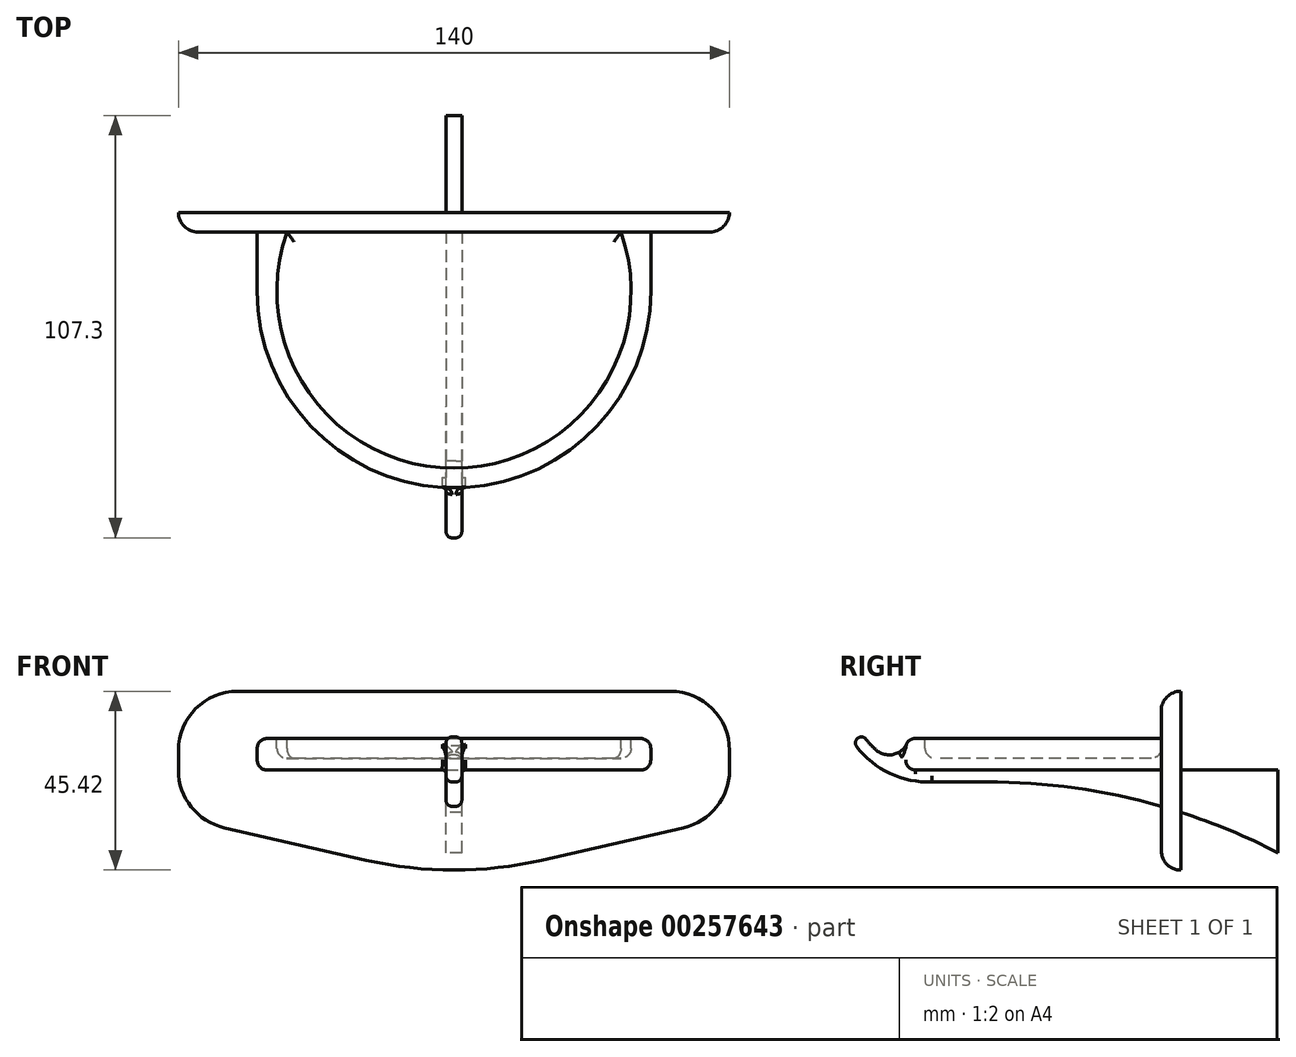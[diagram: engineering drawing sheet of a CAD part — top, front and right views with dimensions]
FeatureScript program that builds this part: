
annotation { "Feature Type Name" : "Feature", "Feature Type Description" : "" }
export const myFeature = defineFeature(function(context is Context, id is Id, definition is map)
    precondition{}
    {
        {
            var Q0;
            Q0=qCreatedBy(makeId("Front.planeOp"),FACE);
            var sketch = newSketch(context, id + "F0", { "sketchPlane" : qUnion([Q0])});
            skLineSegment(sketch, "E0.bottom", {"start": v(-55, 12) * mm, "end": v(55, 12) * mm});
            skLineSegment(sketch, "E0.left", {"start": v(-70, -3) * mm, "end": v(-70, -8.04) * mm});
            skLineSegment(sketch, "E0.right", {"start": v(70, -3) * mm, "end": v(70, -8.04) * mm});
            skLineSegment(sketch, "E1", {"start": v(-58.34, -22.66) * mm, "end": v(-22.28, -30.9) * mm});
            skLineSegment(sketch, "E2", {"start": v(22.28, -30.9) * mm, "end": v(58.34, -22.66) * mm});
            skPoint(sketch, "E3.visualSharp", {"position": v(-70, 12) * mm});
            skArc(sketch, "E3.filletArc", {"start": v(-55, 12) * mm, "mid": v(-65.6, 7.6) * mm, "end": v(-70, -3) * mm});
            skPoint(sketch, "E4.visualSharp", {"position": v(-70, -20) * mm});
            skArc(sketch, "E4.filletArc", {"start": v(-70, -8.04) * mm, "mid": v(-66.73, -17.4) * mm, "end": v(-58.34, -22.66) * mm});
            skPoint(sketch, "E5.visualSharp", {"position": v(70, 12) * mm});
            skArc(sketch, "E5.filletArc", {"start": v(70, -3) * mm, "mid": v(65.6, 7.6) * mm, "end": v(55, 12) * mm});
            skPoint(sketch, "E6.visualSharp", {"position": v(70, -20) * mm});
            skArc(sketch, "E6.filletArc", {"start": v(58.34, -22.66) * mm, "mid": v(66.73, -17.4) * mm, "end": v(70, -8.04) * mm});
            skPoint(sketch, "E7.visualSharp", {"position": v(0, -36) * mm});
            skArc(sketch, "E7.filletArc", {"start": v(-22.28, -30.9) * mm, "mid": v(0, -33.42) * mm, "end": v(22.28, -30.9) * mm});
            skSolve(sketch);
        }
        {
            var Q0;
            Q0=makeQuery(id+"F0.imprint","IMPRINT",FACE,{"disambiguationData":[TD([[makeQuery(id+"F0.imprint","IMPRINT",EDGE,{"derivedFrom":sQuery(id+"F0.wireOp",EDGE,"E0.bottom")}),-1.0]])]});
            extrude(context, id + "F1", {"entities" : qUnion([Q0]), "depth" : 5 * mm});
        }
        {
            var Q0;
            Q0=makeQuery(id+"F1.opExtrude","CAP_EDGE",EDGE,{"disambiguationData":[OSD([sQuery(id+"F0.wireOp",EDGE,"E0.bottom")])],"isStart":false});
            fillet(context, id + "F2", {"entities" : qUnion([Q0]), "radius" : 5 * mm, "tangentPropagation" : true, "allowEdgeOverflow" : false});
        }
        {
            var Q0;
            Q0=qCreatedBy(makeId("Top.planeOp"),FACE);
            var sketch = newSketch(context, id + "F3", { "sketchPlane" : qUnion([Q0])});
            skArc(sketch, "E8", {"start": v(-50, -20) * mm, "mid": v(0, -70) * mm, "end": v(50, -20) * mm});
            skLineSegment(sketch, "E9", {"start": v(50, -5) * mm, "end": v(50, -20) * mm});
            skLineSegment(sketch, "E10", {"start": v(-50, -5) * mm, "end": v(-50, -20) * mm});
            skLineSegment(sketch, "E11", {"start": v(50, -5) * mm, "end": v(-50, -5) * mm});
            skSolve(sketch);
        }
        {
            var Q0;
            Q0=makeQuery(id+"F3.imprint","IMPRINT",FACE,{"disambiguationData":[TD([[makeQuery(id+"F3.imprint","IMPRINT",EDGE,{"derivedFrom":sQuery(id+"F3.wireOp",EDGE,"E8")}),1.0]])]});
            extrude(context, id + "F4", {"entities" : qUnion([Q0]), "operationType" : NewBodyOperationType.ADD, "oppositeDirection" : true, "depth" : 8 * mm});
        }
        {
            var Q0;
            Q0=makeQuery(id+"F4.opExtrude","CAP_FACE",FACE,{"disambiguationData":[OSD([sQuery(id+"F3.wireOp",EDGE,"E8"),sQuery(id+"F3.wireOp",EDGE,"E9"),sQuery(id+"F3.wireOp",EDGE,"E10"),sQuery(id+"F3.wireOp",EDGE,"E11")])],"isStart":true});
            var sketch = newSketch(context, id + "F5", { "sketchPlane" : qUnion([Q0])});
            skArc(sketch, "E12", {"start": v(-42.43, -5) * mm, "mid": v(0, -65) * mm, "end": v(42.43, -5) * mm});
            skLineSegment(sketch, "E13", {"start": v(-42.43, -5) * mm, "end": v(42.43, -5) * mm});
            skSolve(sketch);
        }
        {
            var Q0;
            Q0=makeQuery(id+"F5.imprint","IMPRINT",FACE,{"disambiguationData":[TD([[makeQuery(id+"F5.imprint","IMPRINT",EDGE,{"derivedFrom":sQuery(id+"F5.wireOp",EDGE,"E12")}),1.0]])]});
            extrude(context, id + "F6", {"entities" : qUnion([Q0]), "operationType" : NewBodyOperationType.REMOVE, "oppositeDirection" : true, "depth" : 5 * mm});
        }
        {
            var Q0;
            Q0=makeQuery(id+"F6.boolean.opBoolean","COPY",EDGE,{"derivedFrom":makeQuery(id+"F6.opExtrude","CAP_EDGE",EDGE,{"disambiguationData":[OSD([sQuery(id+"F5.wireOp",EDGE,"E12")])],"isStart":true})});
            var Q1;
            Q1=makeQuery(id+"F4.opExtrude","CAP_EDGE",EDGE,{"disambiguationData":[OSD([sQuery(id+"F3.wireOp",EDGE,"E8")])],"isStart":true});
            var Q2;
            Q2=makeQuery(id+"F4.opExtrude","CAP_EDGE",EDGE,{"disambiguationData":[OSD([sQuery(id+"F3.wireOp",EDGE,"E10")])],"isStart":false});
            var Q3;
            Q3=makeQuery(id+"F6.boolean.opBoolean","COPY",EDGE,{"derivedFrom":makeQuery(id+"F6.opExtrude","CAP_EDGE",EDGE,{"disambiguationData":[OSD([sQuery(id+"F5.wireOp",EDGE,"E12")])],"isStart":false})});
            var Q4;
            Q4=makeQuery(id+"F6.boolean.opBoolean","COPY",EDGE,{"derivedFrom":makeQuery(id+"F6.opExtrude","CAP_EDGE",EDGE,{"disambiguationData":[OSD([sQuery(id+"F5.wireOp",EDGE,"E13")])],"isStart":false})});
            var Q5;
            {var subQ0=sQuery(id+"F3.wireOp",EDGE,"E10");var subQ1=sQuery(id+"F3.wireOp",EDGE,"E11");Q5=makeQuery(id+"F6.boolean.opBoolean","SPLIT",EDGE,{"disambiguationData":[TD([makeQuery(id+"F4.opExtrude","SWEPT_FACE",FACE,{"disambiguationData":[OSD([subQ0])]})])],"derivedFrom":makeQuery(id+"F4.opExtrude","CAP_EDGE",EDGE,{"disambiguationData":[OSD([subQ1])],"isStart":true})});}
            fillet(context, id + "F7", {"entities" : qUnion([Q0, Q1, Q2, Q3, Q4, Q5]), "radius" : 2.5 * mm, "tangentPropagation" : true, "allowEdgeOverflow" : false});
        }
        {
            var Q0;
            Q0=qCreatedBy(makeId("Right.planeOp"),FACE);
            var sketch = newSketch(context, id + "F8", { "sketchPlane" : qUnion([Q0])});
            skArc(sketch, "E14.MirrorCS", {"start": v(-79.99, -0.2) * mm, "mid": v(-82.09, 0.1) * mm, "end": v(-82.39, -2) * mm});
            skArc(sketch, "E15.MirrorCS", {"start": v(-77.35, -3) * mm, "mid": v(-78.75, -1.67) * mm, "end": v(-79.99, -0.2) * mm});
            skArc(sketch, "E16.MirrorCS", {"start": v(-69.83, -1.73) * mm, "mid": v(-73.3, -4.1) * mm, "end": v(-77.35, -3) * mm});
            skLineSegment(sketch, "E17.MirrorCS", {"start": v(-65.39, -8) * mm, "end": v(-69.83, -1.73) * mm});
            skLineSegment(sketch, "E18.MirrorCS", {"start": v(24.61, -29) * mm, "end": v(24.61, -8) * mm});
            skLineSegment(sketch, "E19.MirrorCS", {"start": v(24.61, -8) * mm, "end": v(-65.39, -8) * mm});
            skArc(sketch, "E20", {"start": v(-82.39, -2) * mm, "mid": v(-73.92, -8.9) * mm, "end": v(-63.2, -11) * mm});
            skLineSegment(sketch, "E21", {"start": v(-63.2, -11) * mm, "end": v(-49.37, -11) * mm});
            skArc(sketch, "E22", {"start": v(-49.37, -11) * mm, "mid": v(-11.3, -15.56) * mm, "end": v(24.61, -29) * mm});
            skSolve(sketch);
        }
        {
            var Q0;
            Q0=makeQuery(id+"F8.imprint","IMPRINT",FACE,{"disambiguationData":[TD([[makeQuery(id+"F8.imprint","IMPRINT",EDGE,{"derivedFrom":sQuery(id+"F8.wireOp",EDGE,"E14.MirrorCS")}),1.0]])]});
            extrude(context, id + "F9", {"entities" : qUnion([Q0]), "operationType" : NewBodyOperationType.ADD, "depth" : 4 * mm, "offsetDistance" : 25 * mm, "symmetric" : true});
        }
        {
            var Q0;
            Q0=makeQuery(id+"F9.boolean.opBoolean","INTERSECT",EDGE,{"derivedFrom":[makeQuery(id+"F4.opExtrude","CAP_FACE",FACE,{"disambiguationData":[OSD([sQuery(id+"F3.wireOp",EDGE,"E8"),sQuery(id+"F3.wireOp",EDGE,"E9"),sQuery(id+"F3.wireOp",EDGE,"E10"),sQuery(id+"F3.wireOp",EDGE,"E11")])],"isStart":false}),makeQuery(id+"F9.opExtrude","CAP_FACE",FACE,{"disambiguationData":[OSD([sQuery(id+"F8.wireOp",EDGE,"3d30b8ef-365d-4eac-9476-35001526b1a10.MirrorCS"),sQuery(id+"F8.wireOp",EDGE,"E14.MirrorCS"),sQuery(id+"F8.wireOp",EDGE,"E15.MirrorCS"),sQuery(id+"F8.wireOp",EDGE,"3d30b8ef-365d-4eac-9476-35001526b1a13.MirrorCS"),sQuery(id+"F8.wireOp",EDGE,"3d30b8ef-365d-4eac-9476-35001526b1a14.MirrorCS"),sQuery(id+"F8.wireOp",EDGE,"E16.MirrorCS"),sQuery(id+"F8.wireOp",EDGE,"E17.MirrorCS"),sQuery(id+"F8.wireOp",EDGE,"E18.MirrorCS"),sQuery(id+"F8.wireOp",EDGE,"E19.MirrorCS"),sQuery(id+"F8.wireOp",EDGE,"3d30b8ef-365d-4eac-9476-35001526b1a19.MirrorCS")])],"isStart":true})]});
            var Q1;
            Q1=makeQuery(id+"F9.boolean.opBoolean","INTERSECT",EDGE,{"derivedFrom":[makeQuery(id+"F4.opExtrude","CAP_FACE",FACE,{"disambiguationData":[OSD([sQuery(id+"F3.wireOp",EDGE,"E8"),sQuery(id+"F3.wireOp",EDGE,"E9"),sQuery(id+"F3.wireOp",EDGE,"E10"),sQuery(id+"F3.wireOp",EDGE,"E11")])],"isStart":false}),makeQuery(id+"F9.opExtrude","CAP_FACE",FACE,{"disambiguationData":[OSD([sQuery(id+"F8.wireOp",EDGE,"3d30b8ef-365d-4eac-9476-35001526b1a10.MirrorCS"),sQuery(id+"F8.wireOp",EDGE,"E14.MirrorCS"),sQuery(id+"F8.wireOp",EDGE,"E15.MirrorCS"),sQuery(id+"F8.wireOp",EDGE,"3d30b8ef-365d-4eac-9476-35001526b1a13.MirrorCS"),sQuery(id+"F8.wireOp",EDGE,"3d30b8ef-365d-4eac-9476-35001526b1a14.MirrorCS"),sQuery(id+"F8.wireOp",EDGE,"E16.MirrorCS"),sQuery(id+"F8.wireOp",EDGE,"E17.MirrorCS"),sQuery(id+"F8.wireOp",EDGE,"E18.MirrorCS"),sQuery(id+"F8.wireOp",EDGE,"E19.MirrorCS"),sQuery(id+"F8.wireOp",EDGE,"3d30b8ef-365d-4eac-9476-35001526b1a19.MirrorCS")])],"isStart":false})]});
            fillet(context, id + "F10", {"entities" : qUnion([Q0, Q1]), "radius" : 1 * mm, "tangentPropagation" : true, "allowEdgeOverflow" : false});
        }
        {
            var Q0;
            {var subQ1=sQuery(id+"F8.wireOp",EDGE,"E22");Q0=makeQuery(id+"F9.boolean.opBoolean","SPLIT",EDGE,{"disambiguationData":[TD([makeQuery(id+"F6.opExtrude","SWEPT_FACE",FACE,{"disambiguationData":[OSD([sQuery(id+"F5.wireOp",EDGE,"E13")])]})])],"derivedFrom":makeQuery(id+"F9.opExtrude","CAP_EDGE",EDGE,{"disambiguationData":[OSD([subQ1])],"isStart":true})});}
            var Q1;
            Q1=makeQuery(id+"F9.opExtrude","CAP_EDGE",EDGE,{"disambiguationData":[OSD([sQuery(id+"F8.wireOp",EDGE,"E20")])],"isStart":true});
            var Q2;
            Q2=makeQuery(id+"F9.opExtrude","CAP_EDGE",EDGE,{"disambiguationData":[OSD([sQuery(id+"F8.wireOp",EDGE,"E20")])],"isStart":false});
            fillet(context, id + "F11", {"entities" : qUnion([Q0, Q1, Q2]), "radius" : 1.5 * mm, "tangentPropagation" : true, "allowEdgeOverflow" : false});
        }
    });
